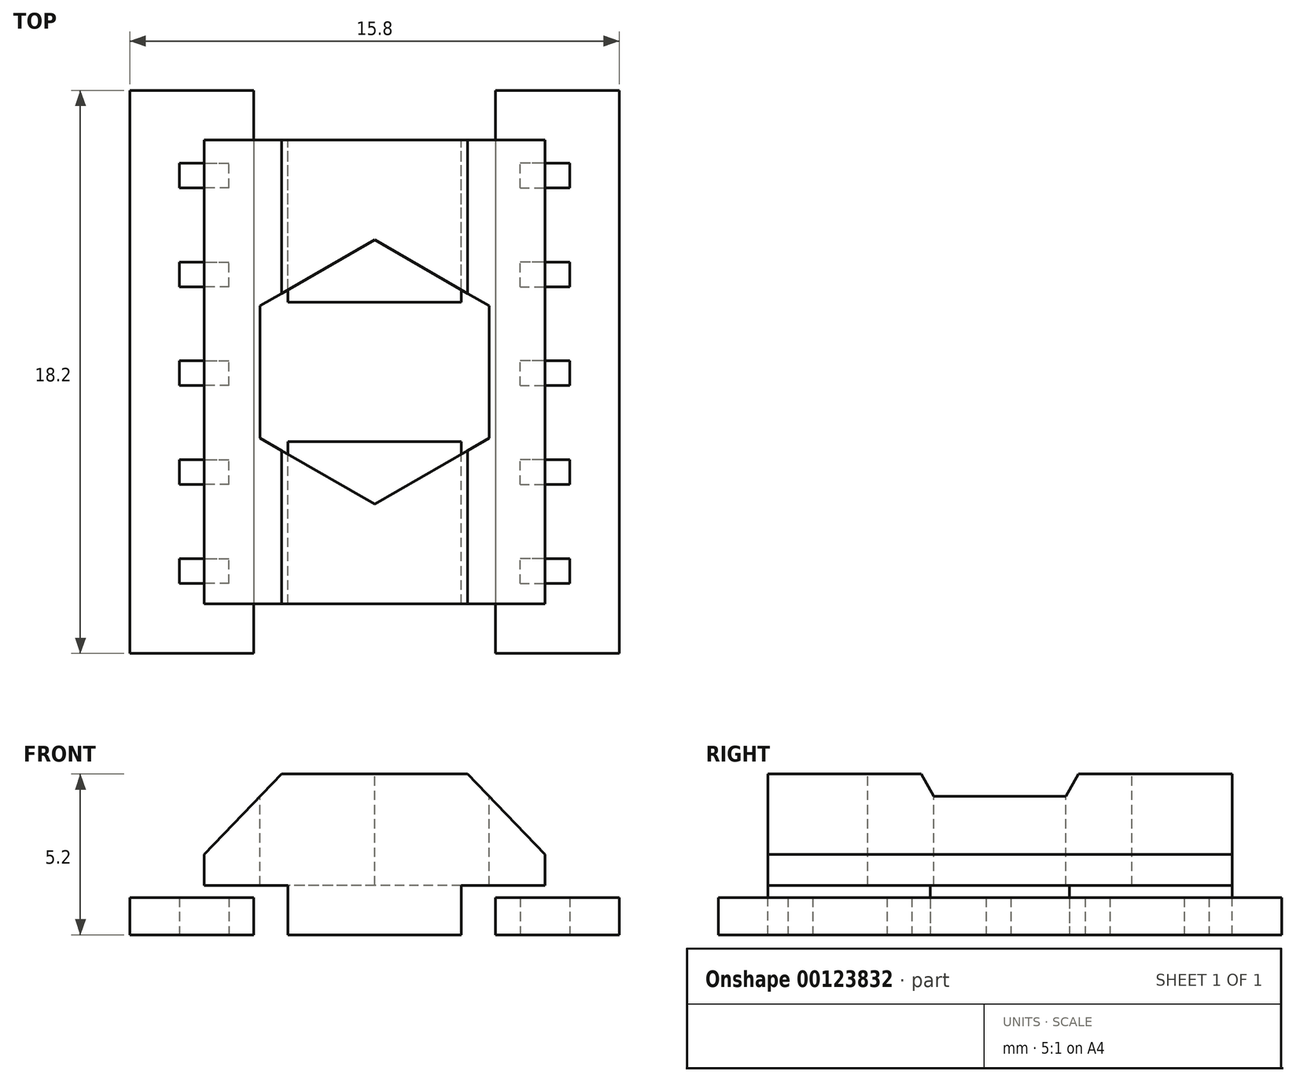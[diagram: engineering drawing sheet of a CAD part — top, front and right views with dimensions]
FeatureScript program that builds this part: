
annotation { "Feature Type Name" : "Feature", "Feature Type Description" : "" }
export const myFeature = defineFeature(function(context is Context, id is Id, definition is map)
    precondition{}
    {
        {
            var Q0;
            Q0=qCreatedBy(makeId("Front.planeOp"),FACE);
            var sketch = newSketch(context, id + "F0", { "sketchPlane" : qUnion([Q0])});
            skLineSegment(sketch, "E0", {"start": v(0, 0) * mm, "end": v(2.8, 0) * mm});
            skLineSegment(sketch, "E1", {"start": v(2.8, 0) * mm, "end": v(2.8, 1.6) * mm});
            skLineSegment(sketch, "E2", {"start": v(2.8, 1.6) * mm, "end": v(5.5, 1.6) * mm});
            skLineSegment(sketch, "E3", {"start": v(5.5, 1.6) * mm, "end": v(5.5, 2.6) * mm});
            skLineSegment(sketch, "E4", {"start": v(5.5, 2.6) * mm, "end": v(3, 5.2) * mm});
            skLineSegment(sketch, "E5", {"start": v(3, 5.2) * mm, "end": v(0, 5.2) * mm});
            skLineSegment(sketch, "E6", {"start": v(0, 0) * mm, "end": v(0, 5.2) * mm, "construction": true});
            skLineSegment(sketch, "E7.MirrorCS", {"start": v(-3, 5.2) * mm, "end": v(0, 5.2) * mm});
            skLineSegment(sketch, "E8.MirrorCS", {"start": v(-5.5, 2.6) * mm, "end": v(-3, 5.2) * mm});
            skLineSegment(sketch, "E9.MirrorCS", {"start": v(-5.5, 1.6) * mm, "end": v(-5.5, 2.6) * mm});
            skLineSegment(sketch, "E10.MirrorCS", {"start": v(-2.8, 1.6) * mm, "end": v(-5.5, 1.6) * mm});
            skLineSegment(sketch, "E11.MirrorCS", {"start": v(-2.8, 0) * mm, "end": v(-2.8, 1.6) * mm});
            skLineSegment(sketch, "E12.MirrorCS", {"start": v(0, 0) * mm, "end": v(-2.8, 0) * mm});
            skSolve(sketch);
        }
        {
            var Q0;
            Q0=makeQuery(id+"F0.imprint","IMPRINT",FACE,{"disambiguationData":[TD([[makeQuery(id+"F0.imprint","IMPRINT",EDGE,{"derivedFrom":sQuery(id+"F0.wireOp",EDGE,"E0")}),1.0]])]});
            extrude(context, id + "F1", {"entities" : qUnion([Q0]), "depth" : 15 * mm});
        }
        {
            var Q0;
            Q0=makeQuery(id+"F1.opExtrude","SWEPT_FACE",FACE,{"disambiguationData":[OSD([sQuery(id+"F0.wireOp",EDGE,"E5"),sQuery(id+"F0.wireOp",EDGE,"E7.MirrorCS")])]});
            var sketch = newSketch(context, id + "F2", { "sketchPlane" : qUnion([Q0])});
            skLineSegment(sketch, "E13", {"start": v(-3, -7.5) * mm, "end": v(3.7, -7.5) * mm, "construction": true});
            skLineSegment(sketch, "E14", {"start": v(0, 0) * mm, "end": v(0, -15) * mm, "construction": true});
            skLineSegment(sketch, "E15", {"start": v(0, -3.23) * mm, "end": v(-3.7, -5.36) * mm});
            skLineSegment(sketch, "E16", {"start": v(-3.7, -5.36) * mm, "end": v(-3.7, -9.64) * mm});
            skLineSegment(sketch, "E17", {"start": v(-3.7, -9.64) * mm, "end": v(0, -11.77) * mm});
            skLineSegment(sketch, "E18", {"start": v(0, -11.77) * mm, "end": v(3.7, -9.64) * mm});
            skLineSegment(sketch, "E19", {"start": v(3.7, -9.64) * mm, "end": v(3.7, -5.36) * mm});
            skLineSegment(sketch, "E20", {"start": v(3.7, -5.36) * mm, "end": v(0, -3.23) * mm});
            skSolve(sketch);
        }
        {
            var Q0;
            {var subQ7=sQuery(id+"F2.wireOp",EDGE,"E20");var subQ8=sQuery(id+"F2.wireOp",EDGE,"E15");var subQ9=makeQuery(id+"F2.imprint","INTERSECT",VERTEX,{"derivedFrom":[subQ8,subQ7]});Q0=makeQuery(id+"F2.imprint","IMPRINT",FACE,{"disambiguationData":[TD([[makeQuery(id+"F2.imprint","IMPRINT",EDGE,{"disambiguationData":[TD([[subQ9,-1.0]])],"derivedFrom":subQ8}),1.0]])]});}
            var Q1;
            {var subQ0=sQuery(id+"F2.wireOp",EDGE,"E19");Q1=makeQuery(id+"F2.imprint","IMPRINT",FACE,{"disambiguationData":[TD([[makeQuery(id+"F2.imprint","IMPRINT",EDGE,{"derivedFrom":subQ0}),1.0]])]});}
            var Q2;
            {var subQ0=sQuery(id+"F2.wireOp",EDGE,"E16");Q2=makeQuery(id+"F2.imprint","IMPRINT",FACE,{"disambiguationData":[TD([[makeQuery(id+"F2.imprint","IMPRINT",EDGE,{"derivedFrom":subQ0}),1.0]])]});}
            var Q3;
            Q3=makeQuery(id+"F1.opExtrude","SWEPT_FACE",FACE,{"disambiguationData":[OSD([sQuery(id+"F0.wireOp",EDGE,"E10.MirrorCS")])]});
            extrude(context, id + "F3", {"entities" : qUnion([Q0, Q1, Q2]), "operationType" : NewBodyOperationType.REMOVE, "endBound" : BoundingType.UP_TO_SURFACE, "oppositeDirection" : true, "endBoundEntityFace" : qUnion([Q3]), "depth" : 3.5 * mm});
        }
        {
            var Q0;
            Q0=qCreatedBy(makeId("Top.planeOp"),FACE);
            var sketch = newSketch(context, id + "F4", { "sketchPlane" : qUnion([Q0])});
            skLineSegment(sketch, "E21", {"start": v(-3.9, 1.6) * mm, "end": v(-3.9, -0.74) * mm});
            skLineSegment(sketch, "E22", {"start": v(-3.9, -16.6) * mm, "end": v(-7.9, -16.6) * mm});
            skLineSegment(sketch, "E23", {"start": v(-7.9, -16.6) * mm, "end": v(-7.9, 1.6) * mm});
            skLineSegment(sketch, "E24", {"start": v(-7.9, 1.6) * mm, "end": v(-3.9, 1.6) * mm});
            skLineSegment(sketch, "E25", {"start": v(0, 0) * mm, "end": v(0, -15) * mm, "construction": true});
            skPoint(sketch, "E26", {"position": v(0, -7.5) * mm});
            skLineSegment(sketch, "E27.bottom", {"start": v(-2.8, -9.75) * mm, "end": v(2.8, -9.75) * mm});
            skLineSegment(sketch, "E27.top", {"start": v(-2.8, -5.25) * mm, "end": v(2.8, -5.25) * mm});
            skLineSegment(sketch, "E27.left", {"start": v(-2.8, -9.75) * mm, "end": v(-2.8, -5.25) * mm});
            skLineSegment(sketch, "E27.right", {"start": v(2.8, -9.75) * mm, "end": v(2.8, -5.25) * mm});
            skLineSegment(sketch, "E28", {"start": v(-4.7, -14.34) * mm, "end": v(-6.3, -14.34) * mm});
            skLineSegment(sketch, "E29", {"start": v(-6.3, -14.34) * mm, "end": v(-6.3, -13.54) * mm});
            skLineSegment(sketch, "E30", {"start": v(-6.3, -13.54) * mm, "end": v(-4.7, -13.54) * mm});
            skLineSegment(sketch, "E31.trimOffspring", {"start": v(-3.9, -14.34) * mm, "end": v(-3.9, -16.6) * mm});
            skLineSegment(sketch, "E32.0.2.0", {"start": v(-4.7, -11.14) * mm, "end": v(-6.3, -11.14) * mm});
            skLineSegment(sketch, "E32.0.2.1", {"start": v(-6.3, -11.14) * mm, "end": v(-6.3, -10.34) * mm});
            skLineSegment(sketch, "E32.0.2.2", {"start": v(-6.3, -10.34) * mm, "end": v(-4.7, -10.34) * mm});
            skLineSegment(sketch, "E32.0.4.0", {"start": v(-4.7, -7.94) * mm, "end": v(-6.3, -7.94) * mm});
            skLineSegment(sketch, "E32.0.4.1", {"start": v(-6.3, -7.94) * mm, "end": v(-6.3, -7.14) * mm});
            skLineSegment(sketch, "E32.0.4.2", {"start": v(-6.3, -7.14) * mm, "end": v(-4.7, -7.14) * mm});
            skLineSegment(sketch, "E32.0.6.0", {"start": v(-4.7, -4.74) * mm, "end": v(-6.3, -4.74) * mm});
            skLineSegment(sketch, "E32.0.6.1", {"start": v(-6.3, -4.74) * mm, "end": v(-6.3, -3.94) * mm});
            skLineSegment(sketch, "E32.0.6.2", {"start": v(-6.3, -3.94) * mm, "end": v(-4.7, -3.94) * mm});
            skLineSegment(sketch, "E32.0.8.0", {"start": v(-4.7, -1.54) * mm, "end": v(-6.3, -1.54) * mm});
            skLineSegment(sketch, "E32.0.8.1", {"start": v(-6.3, -1.54) * mm, "end": v(-6.3, -0.74) * mm});
            skLineSegment(sketch, "E32.0.8.2", {"start": v(-6.3, -0.74) * mm, "end": v(-4.7, -0.74) * mm});
            skLineSegment(sketch, "E32.direction1", {"start": v(-6.3, -13.54) * mm, "end": v(-4.7, -13.54) * mm, "construction": true});
            skLineSegment(sketch, "E33.trimOffspring", {"start": v(-3.9, -12.74) * mm, "end": v(-3.9, -13.54) * mm});
            skLineSegment(sketch, "E34.trimOffspring", {"start": v(-3.9, -11.14) * mm, "end": v(-3.9, -11.94) * mm});
            skLineSegment(sketch, "E35.trimOffspring", {"start": v(-3.9, -9.54) * mm, "end": v(-3.9, -10.34) * mm});
            skLineSegment(sketch, "E36.trimOffspring", {"start": v(-3.9, -7.94) * mm, "end": v(-3.9, -8.74) * mm});
            skLineSegment(sketch, "E37.trimOffspring", {"start": v(-3.9, -1.54) * mm, "end": v(-3.9, -2.34) * mm});
            skLineSegment(sketch, "E38.trimOffspring", {"start": v(-3.9, -3.14) * mm, "end": v(-3.9, -3.94) * mm});
            skLineSegment(sketch, "E39.trimOffspring", {"start": v(-3.9, -4.74) * mm, "end": v(-3.9, -5.54) * mm});
            skLineSegment(sketch, "E40.trimOffspring", {"start": v(-3.9, -6.34) * mm, "end": v(-3.9, -7.14) * mm});
            skLineSegment(sketch, "E41", {"start": v(-3.9, -14.34) * mm, "end": v(-3.9, -0.74) * mm});
            skLineSegment(sketch, "E42", {"start": v(-4.7, -14.34) * mm, "end": v(-4.7, -13.54) * mm});
            skLineSegment(sketch, "E43.trimOffspring", {"start": v(-4.7, -11.14) * mm, "end": v(-4.7, -10.34) * mm});
            skLineSegment(sketch, "E44.trimOffspring", {"start": v(-4.7, -7.94) * mm, "end": v(-4.7, -7.14) * mm});
            skLineSegment(sketch, "E45.trimOffspring", {"start": v(-4.7, -4.74) * mm, "end": v(-4.7, -3.94) * mm});
            skLineSegment(sketch, "E46.trimOffspring", {"start": v(-4.7, -1.54) * mm, "end": v(-4.7, -0.74) * mm});
            skSolve(sketch);
        }
        {
            var Q0;
            Q0=makeQuery(id+"F4.imprint","IMPRINT",FACE,{"disambiguationData":[TD([[makeQuery(id+"F4.imprint","IMPRINT",EDGE,{"derivedFrom":sQuery(id+"F4.wireOp",EDGE,"E21")}),-1.0]])]});
            var Q1;
            Q1=makeQuery(id+"F4.imprint","IMPRINT",FACE,{"disambiguationData":[TD([[makeQuery(id+"F4.imprint","IMPRINT",EDGE,{"derivedFrom":sQuery(id+"F4.wireOp",EDGE,"111994ef-0395-401d-ae35-09e94521523c0.MirrorCS")}),1.0]])]});
            extrude(context, id + "F5", {"entities" : qUnion([Q0, Q1]), "depth" : 1.2 * mm});
        }
        {
            var Q0;
            Q0=makeQuery(id+"F4.imprint","IMPRINT",FACE,{"disambiguationData":[TD([[makeQuery(id+"F4.imprint","IMPRINT",EDGE,{"derivedFrom":sQuery(id+"F4.wireOp",EDGE,"E27.bottom")}),1.0]])]});
            var Q1;
            Q1=makeQuery(id+"F1.opExtrude","SWEPT_FACE",FACE,{"disambiguationData":[OSD([sQuery(id+"F0.wireOp",EDGE,"E10.MirrorCS")])]});
            extrude(context, id + "F6", {"entities" : qUnion([Q0]), "operationType" : NewBodyOperationType.REMOVE, "endBound" : BoundingType.UP_TO_SURFACE, "endBoundEntityFace" : qUnion([Q1]), "depth" : 25 * mm});
        }
        {
            var Q0;
            Q0=makeQuery(id+"F5.opExtrude","SWEPT_BODY",BODY,{"disambiguationData":[OSD([sQuery(id+"F4.wireOp",EDGE,"E21"),sQuery(id+"F4.wireOp",EDGE,"E22"),sQuery(id+"F4.wireOp",EDGE,"E23"),sQuery(id+"F4.wireOp",EDGE,"E24"),sQuery(id+"F4.wireOp",EDGE,"E28"),sQuery(id+"F4.wireOp",EDGE,"E29"),sQuery(id+"F4.wireOp",EDGE,"E30"),sQuery(id+"F4.wireOp",EDGE,"E31.trimOffspring"),sQuery(id+"F4.wireOp",EDGE,"E32.0.1.0"),sQuery(id+"F4.wireOp",EDGE,"E32.0.1.1"),sQuery(id+"F4.wireOp",EDGE,"E32.0.1.2"),sQuery(id+"F4.wireOp",EDGE,"E32.0.2.0"),sQuery(id+"F4.wireOp",EDGE,"E32.0.2.1"),sQuery(id+"F4.wireOp",EDGE,"E32.0.2.2"),sQuery(id+"F4.wireOp",EDGE,"E32.0.3.0"),sQuery(id+"F4.wireOp",EDGE,"E32.0.3.1"),sQuery(id+"F4.wireOp",EDGE,"E32.0.3.2"),sQuery(id+"F4.wireOp",EDGE,"E32.0.4.0"),sQuery(id+"F4.wireOp",EDGE,"E32.0.4.1"),sQuery(id+"F4.wireOp",EDGE,"E32.0.4.2"),sQuery(id+"F4.wireOp",EDGE,"E32.0.5.0"),sQuery(id+"F4.wireOp",EDGE,"E32.0.5.1"),sQuery(id+"F4.wireOp",EDGE,"E32.0.5.2"),sQuery(id+"F4.wireOp",EDGE,"E32.0.6.0"),sQuery(id+"F4.wireOp",EDGE,"E32.0.6.1"),sQuery(id+"F4.wireOp",EDGE,"E32.0.6.2"),sQuery(id+"F4.wireOp",EDGE,"E32.0.7.0"),sQuery(id+"F4.wireOp",EDGE,"E32.0.7.1"),sQuery(id+"F4.wireOp",EDGE,"E32.0.7.2"),sQuery(id+"F4.wireOp",EDGE,"E32.0.8.0"),sQuery(id+"F4.wireOp",EDGE,"E32.0.8.1"),sQuery(id+"F4.wireOp",EDGE,"E32.0.8.2"),sQuery(id+"F4.wireOp",EDGE,"E33.trimOffspring"),sQuery(id+"F4.wireOp",EDGE,"E34.trimOffspring"),sQuery(id+"F4.wireOp",EDGE,"E35.trimOffspring"),sQuery(id+"F4.wireOp",EDGE,"E36.trimOffspring"),sQuery(id+"F4.wireOp",EDGE,"E37.trimOffspring"),sQuery(id+"F4.wireOp",EDGE,"E38.trimOffspring"),sQuery(id+"F4.wireOp",EDGE,"E39.trimOffspring"),sQuery(id+"F4.wireOp",EDGE,"E40.trimOffspring")])]});
            var Q1;
            Q1=qCreatedBy(makeId("Right.planeOp"),FACE);
            mirror(context, id + "F7", {"entities" : qUnion([Q0]), "mirrorPlane" : qUnion([Q1])});
        }
    });
